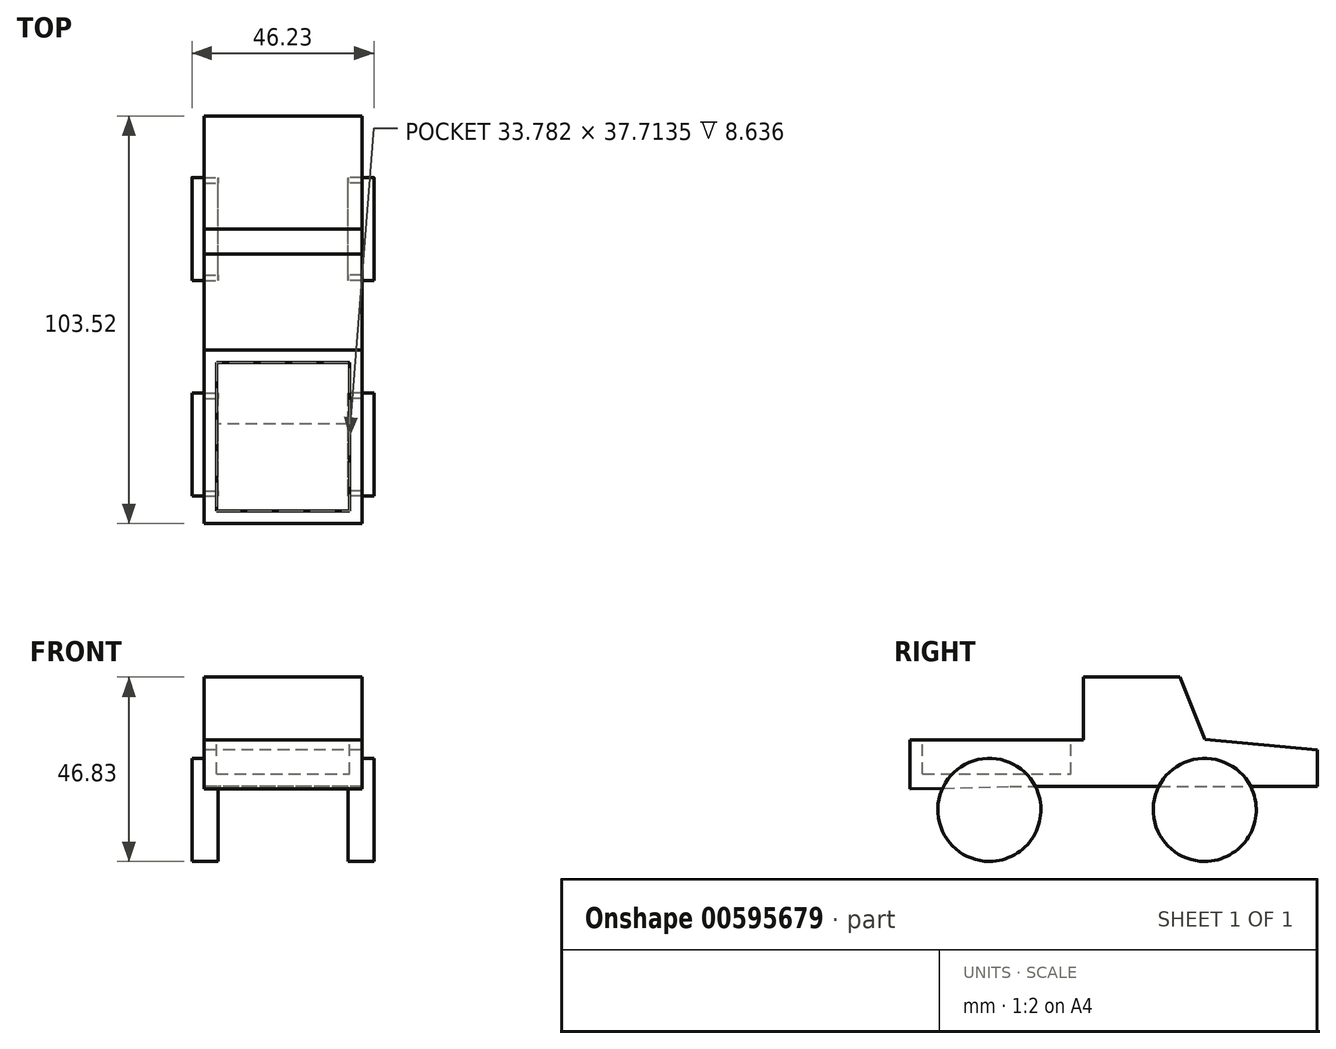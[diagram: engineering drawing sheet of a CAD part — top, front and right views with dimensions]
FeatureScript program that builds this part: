
annotation { "Feature Type Name" : "Feature", "Feature Type Description" : "" }
export const myFeature = defineFeature(function(context is Context, id is Id, definition is map)
    precondition{}
    {
        {
            var Q0;
            Q0=qCreatedBy(makeId("Right.planeOp"),FACE);
            var sketch = newSketch(context, id + "F0", { "sketchPlane" : qUnion([Q0])});
            skLineSegment(sketch, "E0", {"start": v(-54.08, 10.75) * mm, "end": v(24.14, 10.75) * mm});
            skLineSegment(sketch, "E1", {"start": v(24.14, 10.75) * mm, "end": v(24.14, 20.03) * mm});
            skLineSegment(sketch, "E2", {"start": v(24.14, 20.03) * mm, "end": v(-4.53, 22.77) * mm});
            skLineSegment(sketch, "E3", {"start": v(-4.53, 22.77) * mm, "end": v(-10.86, 38.58) * mm});
            skLineSegment(sketch, "E4", {"start": v(-10.86, 38.58) * mm, "end": v(-35.31, 38.58) * mm});
            skLineSegment(sketch, "E5", {"start": v(-35.31, 38.58) * mm, "end": v(-35.31, 22.56) * mm});
            skLineSegment(sketch, "E6", {"start": v(-35.31, 22.56) * mm, "end": v(-79.38, 22.56) * mm});
            skLineSegment(sketch, "E7", {"start": v(-79.38, 22.56) * mm, "end": v(-79.38, 10.12) * mm});
            skLineSegment(sketch, "E8", {"start": v(-79.38, 10.12) * mm, "end": v(-54.08, 10.75) * mm});
            skSolve(sketch);
        }
        {
            var Q0;
            Q0 = qSketchRegion(id + "F0", true);
            extrude(context, id + "F1", {"entities" : qUnion([Q0]), "depth" : 40.13 * mm, "offsetDistance" : 25.4 * mm});
        }
        {
            var Q0;
            Q0=makeQuery(id+"F1.opExtrude","CAP_FACE",FACE,{"disambiguationData":[OSD([sQuery(id+"F0.wireOp",EDGE,"E0"),sQuery(id+"F0.wireOp",EDGE,"E1"),sQuery(id+"F0.wireOp",EDGE,"E2"),sQuery(id+"F0.wireOp",EDGE,"E3"),sQuery(id+"F0.wireOp",EDGE,"E4"),sQuery(id+"F0.wireOp",EDGE,"E5"),sQuery(id+"F0.wireOp",EDGE,"E6"),sQuery(id+"F0.wireOp",EDGE,"E7"),sQuery(id+"F0.wireOp",EDGE,"E8")])],"isStart":false});
            var sketch = newSketch(context, id + "F2", { "sketchPlane" : qUnion([Q0])});
            skCircle(sketch, "E9", {"center": v(-59.24, 4.85) * mm, "radius": 13.1 * mm});
            skCircle(sketch, "E10", {"center": v(-4.53, 4.85) * mm, "radius": 13.1 * mm});
            skSolve(sketch);
        }
        {
            var Q0;
            Q0 = qSketchRegion(id + "F2", true);
            extrude(context, id + "F3", {"entities" : qUnion([Q0]), "operationType" : NewBodyOperationType.ADD, "depth" : 3.05 * mm, "offsetDistance" : 25.4 * mm, "hasSecondDirection" : true, "secondDirectionOppositeDirection" : true, "secondDirectionDepth" : 3.56 * mm});
        }
        {
            var Q0;
            Q0=makeQuery(id+"F1.opExtrude","SWEPT_FACE",FACE,{"disambiguationData":[OSD([sQuery(id+"F0.wireOp",EDGE,"E4")])]});
            var sketch = newSketch(context, id + "F4", { "sketchPlane" : qUnion([Q0])});
            skPoint(sketch, "E11", {"position": v(20.07, -10.86) * mm});
            skSolve(sketch);
        }
        {
            var Q0;
            Q0=qCreatedBy(makeId("Right.planeOp"),FACE);
            var Q1;
            Q1=sQuery(id+"F4.wireOp",VERTEX,"E11");
            cPlane(context, id + "F5", {"entities" : qUnion([Q0, Q1]), "cplaneType" : CPlaneType.PLANE_POINT, "offset" : 25.4 * mm, "width" : 152.4 * mm, "height" : 152.4 * mm});
        }
        {
            var Q0;
            Q0=makeQuery(id+"F1.opExtrude","SWEPT_BODY",BODY,{"disambiguationData":[OSD([sQuery(id+"F0.wireOp",EDGE,"E0"),sQuery(id+"F0.wireOp",EDGE,"E1"),sQuery(id+"F0.wireOp",EDGE,"E2"),sQuery(id+"F0.wireOp",EDGE,"E3"),sQuery(id+"F0.wireOp",EDGE,"E4"),sQuery(id+"F0.wireOp",EDGE,"E5"),sQuery(id+"F0.wireOp",EDGE,"E6"),sQuery(id+"F0.wireOp",EDGE,"E7"),sQuery(id+"F0.wireOp",EDGE,"E8")])]});
            var Q1;
            Q1=qCreatedBy(id+"F5.planeOp",FACE);
            mirror(context, id + "F6", {"operationType" : NewBodyOperationType.ADD, "entities" : qUnion([Q0]), "mirrorPlane" : qUnion([Q1])});
        }
        {
            var Q0;
            Q0=makeQuery(id+"F1.opExtrude","SWEPT_FACE",FACE,{"disambiguationData":[OSD([sQuery(id+"F0.wireOp",EDGE,"E6")])]});
            var sketch = newSketch(context, id + "F7", { "sketchPlane" : qUnion([Q0])});
            skLineSegment(sketch, "E12.0.0", {"start": v(0, -35.31) * mm, "end": v(0, -79.38) * mm, "construction": true});
            skLineSegment(sketch, "E12.0.1", {"start": v(0, -79.38) * mm, "end": v(40.13, -79.38) * mm, "construction": true});
            skLineSegment(sketch, "E12.0.2", {"start": v(40.13, -79.38) * mm, "end": v(40.13, -35.31) * mm, "construction": true});
            skLineSegment(sketch, "E12.0.3", {"start": v(40.13, -35.31) * mm, "end": v(0, -35.31) * mm, "construction": true});
            skLineSegment(sketch, "E13.0", {"start": v(36.96, -76.2) * mm, "end": v(36.96, -38.49) * mm});
            skLineSegment(sketch, "E13.1", {"start": v(3.17, -76.2) * mm, "end": v(36.96, -76.2) * mm});
            skLineSegment(sketch, "E13.2", {"start": v(3.17, -38.49) * mm, "end": v(3.17, -76.2) * mm});
            skLineSegment(sketch, "E13.3", {"start": v(36.96, -38.49) * mm, "end": v(3.17, -38.49) * mm});
            skSolve(sketch);
        }
        {
            var Q0;
            Q0=makeQuery(id+"F7.imprint","IMPRINT",FACE,{"disambiguationData":[TD([[makeQuery(id+"F7.imprint","IMPRINT",EDGE,{"derivedFrom":sQuery(id+"F7.wireOp",EDGE,"E13.0")}),1.0]])]});
            var Q1;
            Q1=sQuery(id+"F7.wireOp",EDGE,"E12.0.2");
            var Q2;
            Q2=sQuery(id+"F7.wireOp",EDGE,"E12.0.3");
            var Q3;
            Q3=sQuery(id+"F7.wireOp",EDGE,"E12.0.0");
            var Q4;
            Q4=sQuery(id+"F7.wireOp",EDGE,"E12.0.1");
            extrude(context, id + "F8", {"entities" : qUnion([Q0]), "operationType" : NewBodyOperationType.REMOVE, "surfaceEntities" : qUnion([Q1, Q2, Q3, Q4]), "oppositeDirection" : true, "depth" : 8.64 * mm, "offsetDistance" : 25.4 * mm});
        }
    });
